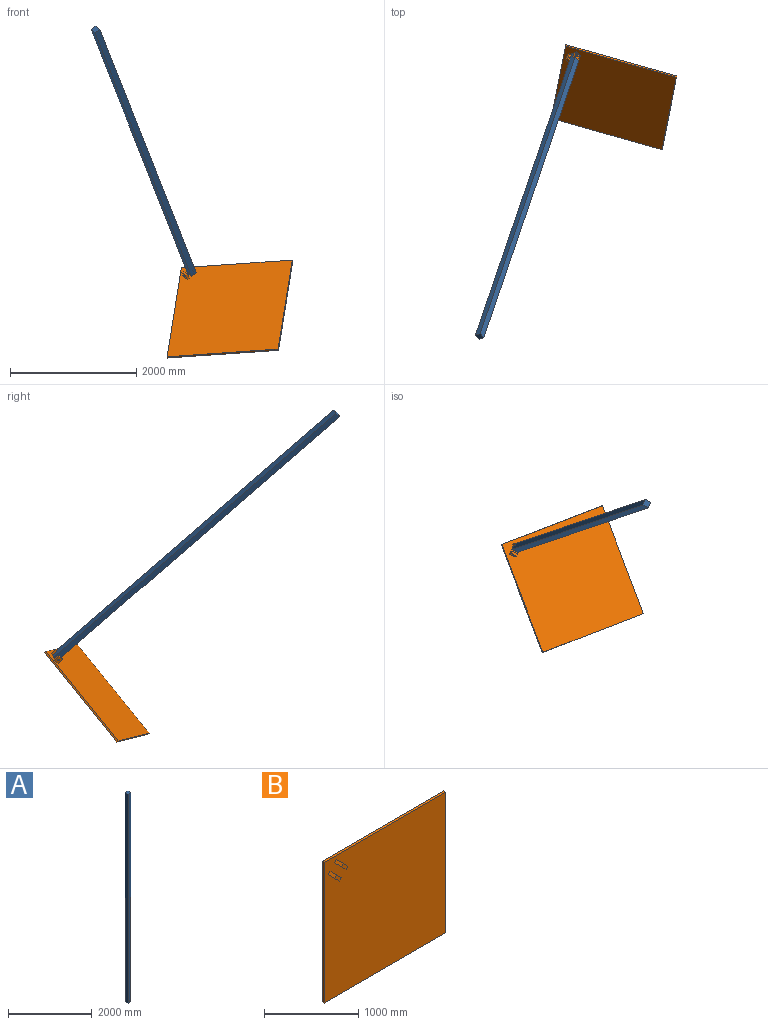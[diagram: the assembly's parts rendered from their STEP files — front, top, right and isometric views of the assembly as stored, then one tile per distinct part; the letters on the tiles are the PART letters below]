
ASSEMBLY  parts=2 mates=2
PART A: 7 faces, bbox 100x100x6096 mm
  f0: plane 6096x100mm, normal (-1,0,0), area 609600mm2, adj f1,f3,f4,f5
  f1: plane 100x100mm, normal (0,0,-1), area 10000mm2, adj f0,f2,f4,f5
  f2: plane 6096x100mm, normal (1,0,0), area 609600mm2, adj f1,f3,f4,f5
  f3: plane 100x100mm, normal (0,0,1), area 10000mm2, adj f0,f2,f4,f5
  f4: plane 6096x100mm, normal (0,-1,0), area 608893.1mm2, adj f0,f1,f2,f3,f6
  f5: plane 6096x100mm, normal (0,1,0), area 608893.1mm2, adj f0,f1,f2,f3,f6
  f6: cylinder r=15mm len=100mm, axis (0,-1,0), area 9424.8mm2, adj f4,f5
PART B: 20 faces, bbox 1828.8x130.5x1828.8 mm
  f0: plane 1828.8x1828.8mm, normal (0,-1,0), area 3336509.4mm2, adj f1,f2,f3,f4,f6,f7,f8,f9
  f1: plane 1828.8x30.48mm, normal (0,0,1), area 55741.8mm2, adj f0,f2,f4,f5
  f2: plane 1828.8x30.48mm, normal (-1,0,0), area 55741.8mm2, adj f0,f1,f3,f5
  f3: plane 1828.8x30.48mm, normal (0,0,-1), area 55741.8mm2, adj f0,f2,f4,f5
  f4: plane 1828.8x30.48mm, normal (1,0,0), area 55741.8mm2, adj f0,f1,f3,f5
  f5: plane 1828.8x1828.8mm, normal (0,1,0), area 3344509.4mm2, adj f1,f2,f3,f4
  f6: plane 100x28.28mm, normal (-0.71,0,0.71), area 4000mm2, adj f0,f7,f9,f10
  f7: plane 100x70.71mm, normal (-0.71,0,-0.71), area 9272.8mm2, adj f0,f6,f8,f10,f18,f19
  f8: plane 100x28.28mm, normal (0.71,0,-0.71), area 4000mm2, adj f0,f7,f9,f10
  f9: plane 100x70.71mm, normal (0.71,0,0.71), area 9272.8mm2, adj f0,f6,f8,f10,f18,f19
  f10: plane 99x99mm, normal (0,-1,0), area 4000mm2, adj f6,f7,f8,f9
  f11: plane 100x70.71mm, normal (0.71,0,0.71), area 9272.8mm2, adj f0,f12,f14,f15,f16,f17
  f12: plane 100x28.28mm, normal (-0.71,0,0.71), area 4000mm2, adj f0,f11,f13,f15
  f13: plane 100x70.71mm, normal (-0.71,0,-0.71), area 9272.8mm2, adj f0,f12,f14,f15,f16,f17
  f14: plane 100x28.28mm, normal (0.71,0,-0.71), area 4000mm2, adj f0,f11,f13,f15
  f15: plane 99x99mm, normal (0,-1,0), area 4000mm2, adj f11,f12,f13,f14
  f16: cylinder r=15mm len=39.13mm, axis (0.71,0,0.71), area 1912.1mm2, adj f11,f13,f17
  f17: cylinder r=15mm len=39.13mm, axis (-0.71,0,-0.71), area 1912.1mm2, adj f11,f13,f16
  f18: cylinder r=15mm len=39.13mm, axis (-0.71,0,-0.71), area 1912.1mm2, adj f7,f9,f19
  f19: cylinder r=15mm len=39.13mm, axis (0.71,0,0.71), area 1912.1mm2, adj f7,f9,f18
PLACE A rot(axis=(0.68,0.13,-0.72),76.3deg) t=(927.57,-2440.37,-1026.66)mm
PLACE B rot(axis=(-0.92,0.04,-0.38),43deg) t=(2217.59,-2602.65,-2102.56)mm
MATE fastened A.f1 <-> A.f6  axis (-0.25,-0.73,0.63) through (1057.79,-1841.04,-1616.99)mm
MATE revolute B.f17 <-> A.f6  axis (0.77,0.25,0.59) through (1088.86,-1807.32,-1502.55)mm
